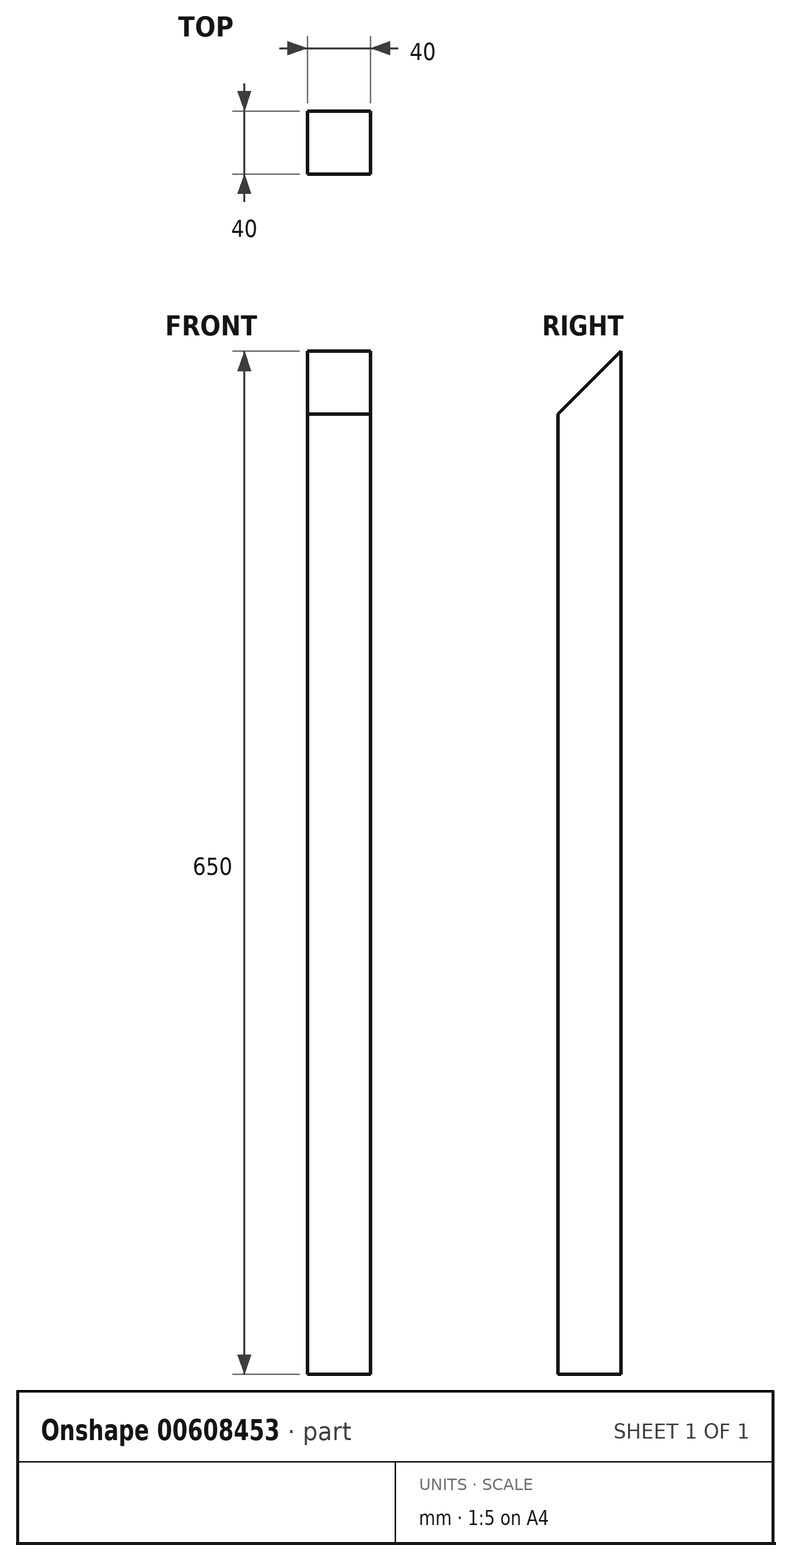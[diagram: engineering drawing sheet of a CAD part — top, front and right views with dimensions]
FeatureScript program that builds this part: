
annotation { "Feature Type Name" : "Feature", "Feature Type Description" : "" }
export const myFeature = defineFeature(function(context is Context, id is Id, definition is map)
    precondition{}
    {
        {
            var Q0;
            Q0=qCreatedBy(makeId("Right.planeOp"),FACE);
            var sketch = newSketch(context, id + "F0", { "sketchPlane" : qUnion([Q0])});
            skLineSegment(sketch, "E0.top", {"start": v(-43.27, -410.38) * mm, "end": v(-3.27, -410.38) * mm});
            skLineSegment(sketch, "E0.left", {"start": v(-43.27, 199.62) * mm, "end": v(-43.27, -410.38) * mm});
            skLineSegment(sketch, "E0.right", {"start": v(-3.27, 239.62) * mm, "end": v(-3.27, -410.38) * mm});
            skLineSegment(sketch, "E1", {"start": v(-3.27, 239.62) * mm, "end": v(-43.27, 199.62) * mm});
            skSolve(sketch);
        }
        {
            var Q0;
            Q0=makeQuery(id+"F0.imprint","IMPRINT",FACE,{"disambiguationData":[TD([[makeQuery(id+"F0.imprint","IMPRINT",EDGE,{"derivedFrom":sQuery(id+"F0.wireOp",EDGE,"E0.top")}),1.0]])]});
            extrude(context, id + "F1", {"entities" : qUnion([Q0]), "depth" : 40 * mm, "offsetDistance" : 25 * mm});
        }
    });
